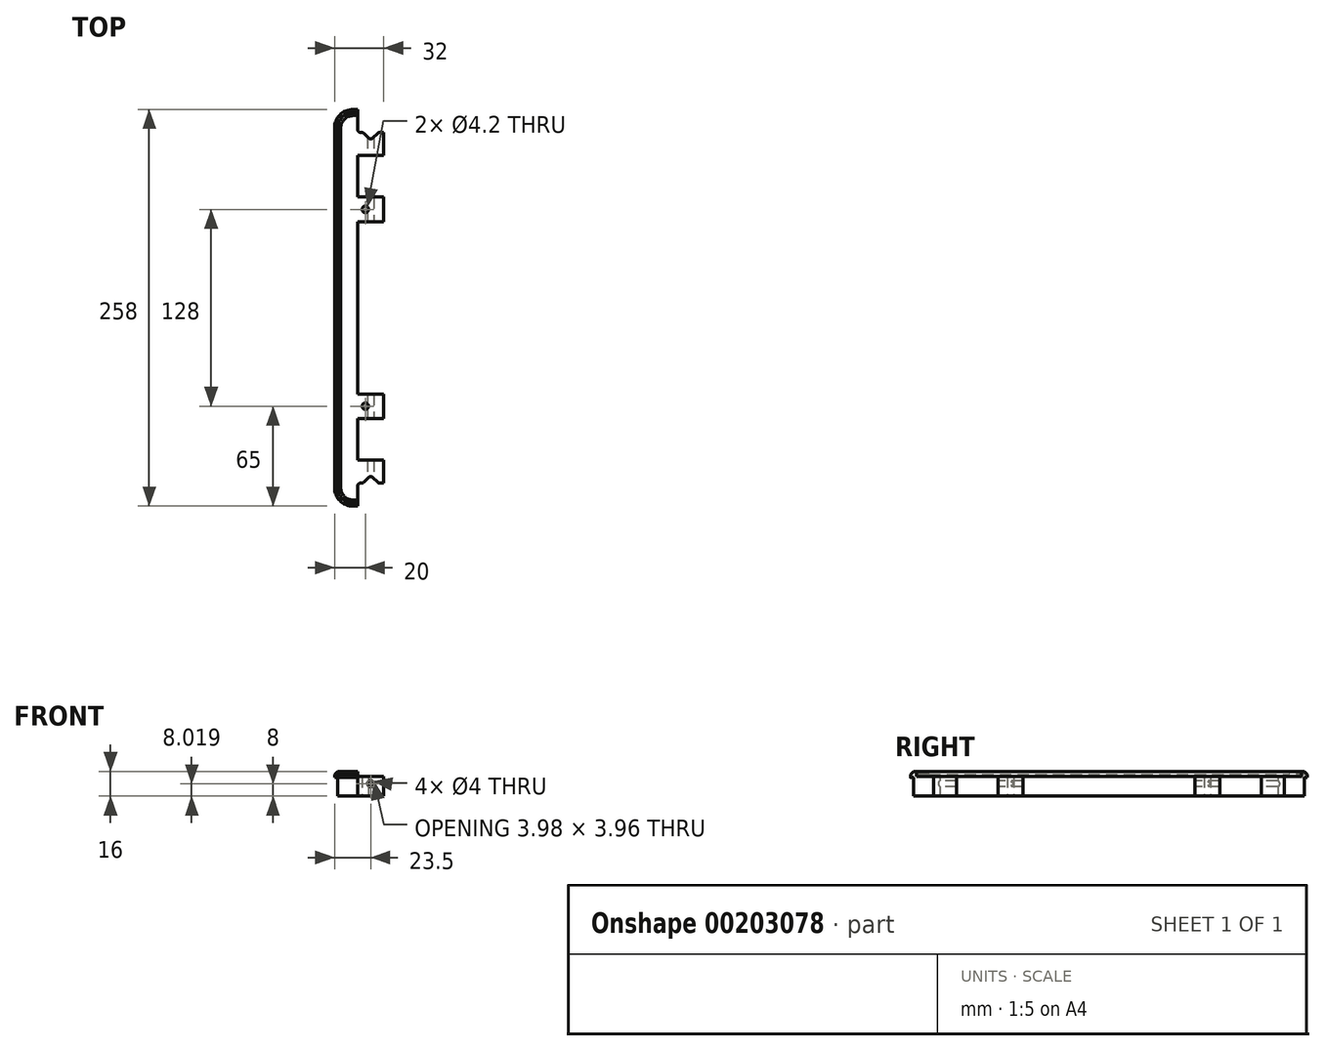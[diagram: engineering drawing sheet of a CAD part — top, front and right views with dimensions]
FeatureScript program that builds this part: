
annotation { "Feature Type Name" : "Feature", "Feature Type Description" : "" }
export const myFeature = defineFeature(function(context is Context, id is Id, definition is map)
    precondition{}
    {
        {
            var Q0;
            Q0=qCreatedBy(makeId("Top.planeOp"),FACE);
            var sketch = newSketch(context, id + "F0", { "sketchPlane" : qUnion([Q0])});
            skLineSegment(sketch, "E0.bottom", {"start": v(-174.5, 129) * mm, "end": v(-171.5, 129) * mm});
            skLineSegment(sketch, "E0.top", {"start": v(-174.5, -129) * mm, "end": v(-171.5, -129) * mm});
            skLineSegment(sketch, "E0.left", {"start": v(-186.5, 117) * mm, "end": v(-186.5, -117) * mm});
            skPoint(sketch, "E1.visualSharp", {"position": v(-186.5, -129) * mm});
            skArc(sketch, "E1.filletArc", {"start": v(-186.5, -117) * mm, "mid": v(-182.99, -125.49) * mm, "end": v(-174.5, -129) * mm});
            skPoint(sketch, "E2.visualSharp", {"position": v(-186.5, 129) * mm});
            skArc(sketch, "E2.filletArc", {"start": v(-174.5, 129) * mm, "mid": v(-182.99, 125.49) * mm, "end": v(-186.5, 117) * mm});
            skLineSegment(sketch, "E3.left", {"start": v(-171.5, 99) * mm, "end": v(-171.5, 72) * mm});
            skLineSegment(sketch, "E4.bottom", {"start": v(-171.5, 72) * mm, "end": v(-154.5, 72) * mm});
            skLineSegment(sketch, "E4.top", {"start": v(-171.5, 56) * mm, "end": v(-154.5, 56) * mm});
            skLineSegment(sketch, "E4.right", {"start": v(-154.5, 72) * mm, "end": v(-154.5, 56) * mm});
            skLineSegment(sketch, "E5.trimOffspring", {"start": v(-171.5, 56) * mm, "end": v(-171.5, -56) * mm});
            skLineSegment(sketch, "E6.MirrorCS", {"start": v(-171.5, -56) * mm, "end": v(-154.5, -56) * mm});
            skLineSegment(sketch, "E7.MirrorCS", {"start": v(-154.5, -72) * mm, "end": v(-154.5, -56) * mm});
            skLineSegment(sketch, "E8.MirrorCS", {"start": v(-171.5, -72) * mm, "end": v(-154.5, -72) * mm});
            skLineSegment(sketch, "E9.trimOffspring", {"start": v(-171.5, -72) * mm, "end": v(-171.5, -99) * mm});
            skCircle(sketch, "E10", {"center": v(-166.5, 64) * mm, "radius": 2.1 * mm});
            skCircle(sketch, "E11.MirrorC", {"center": v(-166.5, -64) * mm, "radius": 2.1 * mm});
            skLineSegment(sketch, "E12.top", {"start": v(-171.5, 99) * mm, "end": v(-154.5, 99) * mm});
            skLineSegment(sketch, "E12.right", {"start": v(-154.5, 114) * mm, "end": v(-154.5, 99) * mm});
            skLineSegment(sketch, "E13.MirrorCS", {"start": v(-171.5, -99) * mm, "end": v(-154.5, -99) * mm});
            skLineSegment(sketch, "E14.MirrorCS", {"start": v(-154.5, -114) * mm, "end": v(-154.5, -99) * mm});
            skLineSegment(sketch, "E15", {"start": v(-154.5, -114) * mm, "end": v(-157.17, -114) * mm});
            skLineSegment(sketch, "E16", {"start": v(-158.59, -113.41) * mm, "end": v(-161.59, -110.41) * mm});
            skLineSegment(sketch, "E17", {"start": v(-164.41, -110.41) * mm, "end": v(-167.41, -113.41) * mm});
            skLineSegment(sketch, "E18", {"start": v(-168.83, -114) * mm, "end": v(-169.5, -114) * mm});
            skLineSegment(sketch, "E19", {"start": v(-171.5, -116) * mm, "end": v(-171.5, -127.73) * mm});
            skPoint(sketch, "E20.visualSharp", {"position": v(-163, -109) * mm});
            skArc(sketch, "E20.filletArc", {"start": v(-161.59, -110.41) * mm, "mid": v(-163, -109.83) * mm, "end": v(-164.41, -110.41) * mm});
            skPoint(sketch, "E21.visualSharp", {"position": v(-158, -114) * mm});
            skArc(sketch, "E21.filletArc", {"start": v(-158.59, -113.41) * mm, "mid": v(-157.94, -113.85) * mm, "end": v(-157.17, -114) * mm});
            skPoint(sketch, "E22.visualSharp", {"position": v(-168, -114) * mm});
            skArc(sketch, "E22.filletArc", {"start": v(-168.83, -114) * mm, "mid": v(-168.06, -113.85) * mm, "end": v(-167.41, -113.41) * mm});
            skPoint(sketch, "E23.visualSharp", {"position": v(-171.5, -114) * mm});
            skArc(sketch, "E23.filletArc", {"start": v(-169.5, -114) * mm, "mid": v(-170.91, -114.59) * mm, "end": v(-171.5, -116) * mm});
            skLineSegment(sketch, "E24", {"start": v(-171.5, -127.73) * mm, "end": v(-171.5, -129) * mm});
            skLineSegment(sketch, "E25.MirrorCS", {"start": v(-154.5, 114) * mm, "end": v(-157.17, 114) * mm});
            skArc(sketch, "E26.MirrorCS", {"start": v(-158.59, 113.41) * mm, "mid": v(-157.94, 113.85) * mm, "end": v(-157.17, 114) * mm});
            skLineSegment(sketch, "E27.MirrorCS", {"start": v(-158.59, 113.41) * mm, "end": v(-161.59, 110.41) * mm});
            skArc(sketch, "E28.MirrorCS", {"start": v(-161.59, 110.41) * mm, "mid": v(-163, 109.83) * mm, "end": v(-164.41, 110.41) * mm});
            skLineSegment(sketch, "E29.MirrorCS", {"start": v(-164.41, 110.41) * mm, "end": v(-167.41, 113.41) * mm});
            skArc(sketch, "E30.MirrorCS", {"start": v(-168.83, 114) * mm, "mid": v(-168.06, 113.85) * mm, "end": v(-167.41, 113.41) * mm});
            skLineSegment(sketch, "E31.MirrorCS", {"start": v(-168.83, 114) * mm, "end": v(-169.5, 114) * mm});
            skArc(sketch, "E32.MirrorCS", {"start": v(-169.5, 114) * mm, "mid": v(-170.91, 114.59) * mm, "end": v(-171.5, 116) * mm});
            skLineSegment(sketch, "E33.MirrorCS", {"start": v(-171.5, 116) * mm, "end": v(-171.5, 127.73) * mm});
            skLineSegment(sketch, "E34", {"start": v(-171.5, 127.73) * mm, "end": v(-171.5, 129) * mm});
            skSolve(sketch);
        }
        {
            var Q0;
            Q0=makeQuery(id+"F0.imprint","IMPRINT",FACE,{"disambiguationData":[TD([[makeQuery(id+"F0.imprint","IMPRINT",EDGE,{"derivedFrom":sQuery(id+"F0.wireOp",EDGE,"E0.bottom")}),-1.0]])]});
            extrude(context, id + "F1", {"entities" : qUnion([Q0]), "depth" : 16 * mm});
        }
        {
            var Q0;
            Q0=makeQuery(id+"F1.opExtrude","CAP_EDGE",EDGE,{"disambiguationData":[OSD([sQuery(id+"F0.wireOp",EDGE,"E0.top")])],"isStart":false});
            chamfer(context, id + "F2", {"entities" : qUnion([Q0]), "width" : 2 * mm, "tangentPropagation" : true});
        }
        {
            var Q0;
            Q0=makeQuery(id+"F1.opExtrude","CAP_FACE",FACE,{"disambiguationData":[OSD([sQuery(id+"F0.wireOp",EDGE,"E0.bottom"),sQuery(id+"F0.wireOp",EDGE,"E0.top"),sQuery(id+"F0.wireOp",EDGE,"E0.left"),sQuery(id+"F0.wireOp",EDGE,"E0.right"),sQuery(id+"F0.wireOp",EDGE,"E1.filletArc"),sQuery(id+"F0.wireOp",EDGE,"E2.filletArc"),sQuery(id+"F0.wireOp",EDGE,"0606984b-c95c-4b6f-a22b-b9101ec73185.filletArc"),sQuery(id+"F0.wireOp",EDGE,"ed30f497-0052-4637-aeee-16b670f2d78a.filletArc"),sQuery(id+"F0.wireOp",EDGE,"E3.bottom"),sQuery(id+"F0.wireOp",EDGE,"E3.top"),sQuery(id+"F0.wireOp",EDGE,"E3.left"),sQuery(id+"F0.wireOp",EDGE,"E3.right")])],"isStart":false});
            var sketch = newSketch(context, id + "F3", { "sketchPlane" : qUnion([Q0])});
            skLineSegment(sketch, "E35.0", {"start": v(-182.5, 117) * mm, "end": v(-182.5, -117) * mm});
            skLineSegment(sketch, "E35.1", {"start": v(-153.81, 125) * mm, "end": v(-174.5, 125) * mm});
            skLineSegment(sketch, "E35.3", {"start": v(-174.5, -125) * mm, "end": v(-154.5, -125) * mm});
            skPoint(sketch, "E36.visualSharp", {"position": v(-182.5, -125) * mm});
            skArc(sketch, "E36.filletArc", {"start": v(-182.5, -117) * mm, "mid": v(-180.16, -122.66) * mm, "end": v(-174.5, -125) * mm});
            skPoint(sketch, "E37.visualSharp", {"position": v(-182.5, 125) * mm});
            skArc(sketch, "E37.filletArc", {"start": v(-174.5, 125) * mm, "mid": v(-180.16, 122.66) * mm, "end": v(-182.5, 117) * mm});
            skLineSegment(sketch, "E38", {"start": v(-153.81, 125) * mm, "end": v(-154.5, -125) * mm});
            skSolve(sketch);
        }
        {
            var Q0;
            Q0 = qSketchRegion(id + "F3", true);
            extrude(context, id + "F4", {"entities" : qUnion([Q0]), "operationType" : NewBodyOperationType.REMOVE, "oppositeDirection" : true, "depth" : 3.1 * mm});
        }
        {
            var Q0;
            Q0=makeQuery(id+"F0.imprint","IMPRINT",FACE,{"disambiguationData":[TD([[makeQuery(id+"F0.imprint","IMPRINT",EDGE,{"derivedFrom":sQuery(id+"F0.wireOp",EDGE,"E0.bottom")}),-1.0]])]});
            var sketch = newSketch(context, id + "F5", { "sketchPlane" : qUnion([Q0])});
            skLineSegment(sketch, "E39.1", {"start": v(-172.6, 127.1) * mm, "end": v(-152.2, 127.1) * mm});
            skLineSegment(sketch, "E39.2", {"start": v(-184.6, 115.1) * mm, "end": v(-184.6, -115.1) * mm});
            skLineSegment(sketch, "E39.5", {"start": v(-172.6, -127.1) * mm, "end": v(-152.2, -127.1) * mm});
            skArc(sketch, "E40.filletArc", {"start": v(-184.6, -115.1) * mm, "mid": v(-181.09, -123.59) * mm, "end": v(-172.6, -127.1) * mm});
            skArc(sketch, "E41.filletArc", {"start": v(-172.6, 127.1) * mm, "mid": v(-181.09, 123.59) * mm, "end": v(-184.6, 115.1) * mm});
            skArc(sketch, "E42.0", {"start": v(-172.6, 132.1) * mm, "mid": v(-184.62, 127.12) * mm, "end": v(-189.6, 115.1) * mm});
            skLineSegment(sketch, "E42.1", {"start": v(-172.6, 132.1) * mm, "end": v(-152.2, 132.1) * mm});
            skLineSegment(sketch, "E42.2", {"start": v(-189.6, 115.1) * mm, "end": v(-189.6, -115.1) * mm});
            skArc(sketch, "E42.4", {"start": v(-189.6, -115.1) * mm, "mid": v(-184.62, -127.12) * mm, "end": v(-172.6, -132.1) * mm});
            skLineSegment(sketch, "E42.5", {"start": v(-172.6, -132.1) * mm, "end": v(-152.2, -132.1) * mm});
            skLineSegment(sketch, "E43", {"start": v(-152.2, 132.1) * mm, "end": v(-152.2, 127.1) * mm});
            skLineSegment(sketch, "E44.MirrorCS", {"start": v(-152.2, -132.1) * mm, "end": v(-152.2, -127.1) * mm});
            skSolve(sketch);
        }
        {
            var Q0;
            Q0 = qSketchRegion(id + "F5", true);
            extrude(context, id + "F6", {"entities" : qUnion([Q0]), "operationType" : NewBodyOperationType.REMOVE, "depth" : 12 * mm});
        }
        {
            var Q0;
            Q0=makeQuery(id+"F6.boolean.opBoolean","COPY",FACE,{"derivedFrom":makeQuery(id+"F6.opExtrude","SWEPT_FACE",FACE,{"disambiguationData":[OSD([sQuery(id+"F5.wireOp",EDGE,"E39.5")])]})});
            var sketch = newSketch(context, id + "F7", { "sketchPlane" : qUnion([Q0])});
            skCircle(sketch, "E45", {"center": v(-163, 8) * mm, "radius": 2 * mm});
            skCircle(sketch, "E46.MirrorC", {"center": v(163, 8) * mm, "radius": 2 * mm});
            skSolve(sketch);
        }
        {
            var Q0;
            Q0 = qSketchRegion(id + "F7", true);
            extrude(context, id + "F8", {"entities" : qUnion([Q0]), "operationType" : NewBodyOperationType.REMOVE, "endBound" : BoundingType.THROUGH_ALL, "oppositeDirection" : true, "depth" : 25 * mm});
        }
    });
